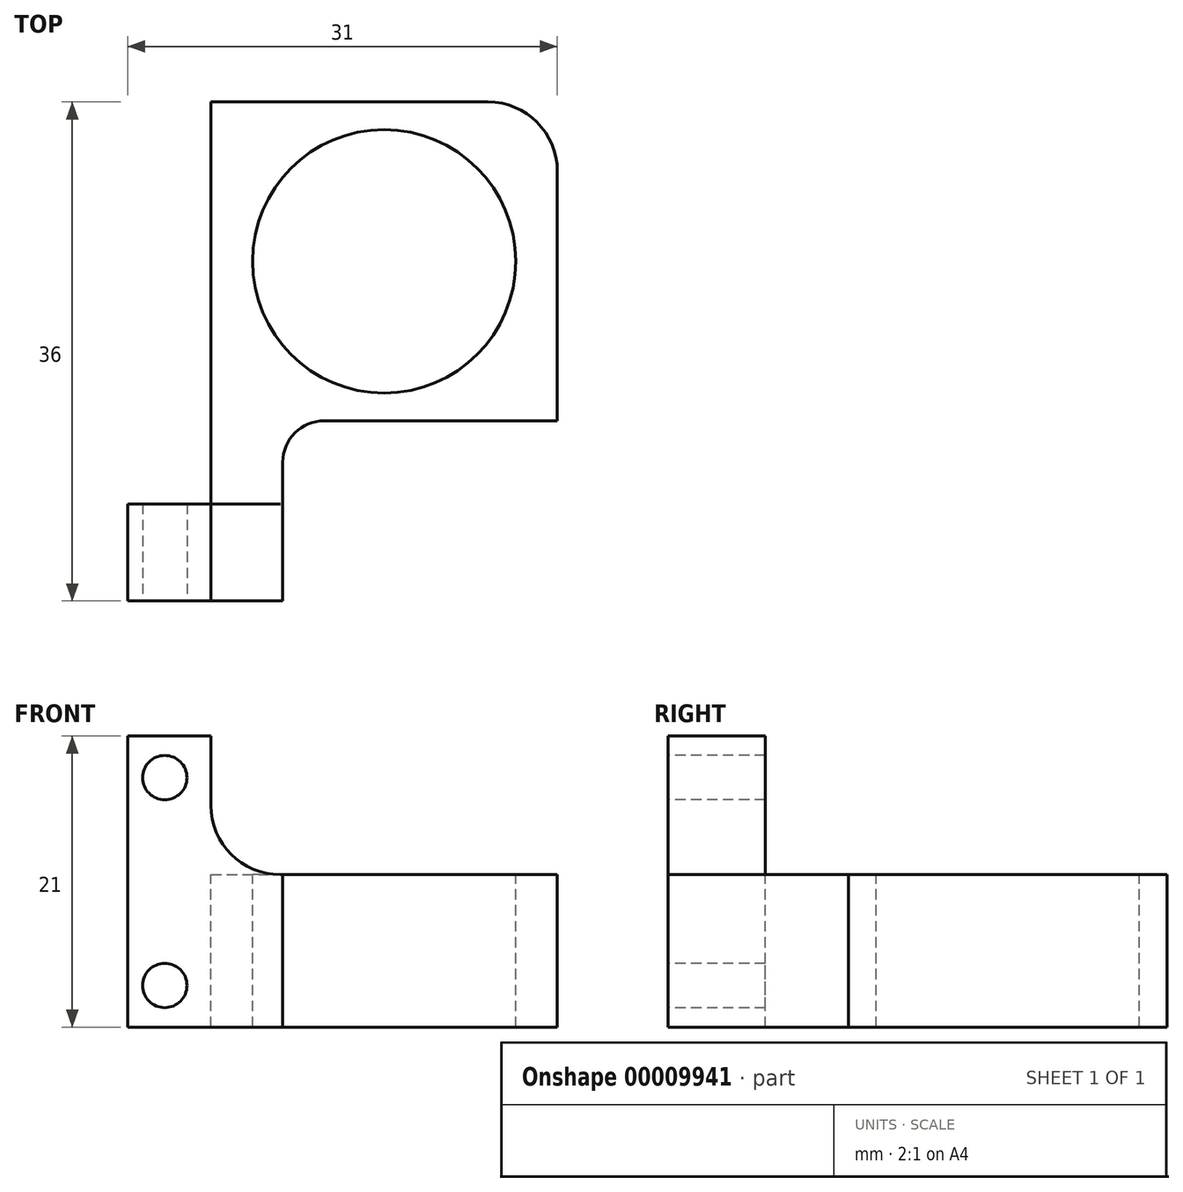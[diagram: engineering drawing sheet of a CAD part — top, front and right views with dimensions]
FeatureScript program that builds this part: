
annotation { "Feature Type Name" : "Feature", "Feature Type Description" : "" }
export const myFeature = defineFeature(function(context is Context, id is Id, definition is map)
    precondition{}
    {
        {
            var Q0;
            Q0=qCreatedBy(makeId("Top.planeOp"),FACE);
            var sketch = newSketch(context, id + "F0", { "sketchPlane" : qUnion([Q0])});
            skLineSegment(sketch, "E0.bottom", {"start": v(0, 0) * mm, "end": v(31, 0) * mm});
            skLineSegment(sketch, "E0.top", {"start": v(0, 36) * mm, "end": v(31, 36) * mm});
            skLineSegment(sketch, "E0.left", {"start": v(0, 0) * mm, "end": v(0, 36) * mm});
            skLineSegment(sketch, "E0.right", {"start": v(31, 0) * mm, "end": v(31, 36) * mm});
            skSolve(sketch);
        }
        {
            var Q0;
            Q0 = qSketchRegion(id + "F0", true);
            extrude(context, id + "F1", {"entities" : qUnion([Q0]), "depth" : 4 * mm});
        }
        {
            var Q0;
            Q0=makeQuery(id+"F1.opExtrude","CAP_FACE",FACE,{"disambiguationData":[OSD([sQuery(id+"F0.wireOp",EDGE,"E0.bottom"),sQuery(id+"F0.wireOp",EDGE,"E0.top"),sQuery(id+"F0.wireOp",EDGE,"E0.left"),sQuery(id+"F0.wireOp",EDGE,"E0.right")])],"isStart":false});
            var sketch = newSketch(context, id + "F2", { "sketchPlane" : qUnion([Q0])});
            skCircle(sketch, "E1", {"center": v(18.5, 24.5) * mm, "radius": 9.5 * mm});
            skLineSegment(sketch, "E2.bottom", {"start": v(0, 36) * mm, "end": v(6, 36) * mm});
            skLineSegment(sketch, "E2.top", {"start": v(0, 7) * mm, "end": v(6, 7) * mm});
            skLineSegment(sketch, "E2.left", {"start": v(0, 36) * mm, "end": v(0, 7) * mm});
            skLineSegment(sketch, "E2.right", {"start": v(6, 36) * mm, "end": v(6, 7) * mm});
            skLineSegment(sketch, "E3.bottom", {"start": v(31, 0) * mm, "end": v(11.18, 0) * mm});
            skLineSegment(sketch, "E3.top", {"start": v(31, 13) * mm, "end": v(11.18, 13) * mm});
            skLineSegment(sketch, "E3.left", {"start": v(31, 0) * mm, "end": v(31, 13) * mm});
            skLineSegment(sketch, "E3.right", {"start": v(11.18, 0) * mm, "end": v(11.18, 13) * mm});
            skSolve(sketch);
        }
        {
            var Q0;
            Q0 = qSketchRegion(id + "F2", true);
            extrude(context, id + "F3", {"entities" : qUnion([Q0]), "operationType" : NewBodyOperationType.REMOVE, "oppositeDirection" : true, "depth" : 25 * mm});
        }
        {
            var Q0;
            Q0=makeQuery(id+"F1.opExtrude","CAP_FACE",FACE,{"disambiguationData":[OSD([sQuery(id+"F0.wireOp",EDGE,"E0.bottom"),sQuery(id+"F0.wireOp",EDGE,"E0.top"),sQuery(id+"F0.wireOp",EDGE,"E0.left"),sQuery(id+"F0.wireOp",EDGE,"E0.right")])],"isStart":false});
            var sketch = newSketch(context, id + "F4", { "sketchPlane" : qUnion([Q0])});
            skLineSegment(sketch, "E4.bottom", {"start": v(0, 7) * mm, "end": v(6, 7) * mm});
            skLineSegment(sketch, "E4.top", {"start": v(0, 0) * mm, "end": v(6, 0) * mm});
            skLineSegment(sketch, "E4.left", {"start": v(0, 7) * mm, "end": v(0, 0) * mm});
            skLineSegment(sketch, "E4.right", {"start": v(6, 7) * mm, "end": v(6, 0) * mm});
            skSolve(sketch);
        }
        {
            var Q0;
            Q0 = qSketchRegion(id + "F4", true);
            var Q1;
            {var subQ1=sQuery(id+"F4.wireOp",EDGE,"E4.right");Q1=makeQuery(id+"F4.imprint","IMPRINT",FACE,{"disambiguationData":[TD([[makeQuery(id+"F4.imprint","IMPRINT",EDGE,{"derivedFrom":subQ1}),1.0]])]});}
            extrude(context, id + "F5", {"entities" : qUnion([Q0, Q1]), "operationType" : NewBodyOperationType.ADD, "depth" : 7 * mm});
        }
        {
            var Q0;
            Q0=makeQuery(id+"F4.imprint","IMPRINT",FACE,{"disambiguationData":[TD([[makeQuery(id+"F4.imprint","IMPRINT",EDGE,{"derivedFrom":sQuery(id+"F4.wireOp",EDGE,"E4.bottom")}),-1.0]])]});
            extrude(context, id + "F6", {"entities" : qUnion([Q0]), "operationType" : NewBodyOperationType.ADD, "depth" : 17 * mm});
        }
        {
            var Q0;
            Q0=makeQuery(id+"F5.boolean.opBoolean","MERGE",FACE,{"derivedFrom":[makeQuery(id+"F1.opExtrude","SWEPT_FACE",FACE,{"disambiguationData":[OSD([sQuery(id+"F0.wireOp",EDGE,"E0.bottom")])]}),makeQuery(id+"F5.opExtrude","SWEPT_FACE",FACE,{"disambiguationData":[OSD([sQuery(id+"F4.wireOp",EDGE,"E4.top")])]})]});
            var sketch = newSketch(context, id + "F7", { "sketchPlane" : qUnion([Q0])});
            skLineSegment(sketch, "E5", {"start": v(2.68, 18) * mm, "end": v(2.68, 3) * mm});
            skCircle(sketch, "E6", {"center": v(2.68, 18) * mm, "radius": 1.6 * mm});
            skCircle(sketch, "E7", {"center": v(2.68, 3) * mm, "radius": 1.6 * mm});
            skSolve(sketch);
        }
        {
            var Q0;
            Q0 = qSketchRegion(id + "F7", true);
            extrude(context, id + "F8", {"entities" : qUnion([Q0]), "operationType" : NewBodyOperationType.REMOVE, "oppositeDirection" : true, "depth" : 25 * mm});
        }
        {
            var Q0;
            Q0=makeQuery(id+"F1.opExtrude","SWEPT_EDGE",EDGE,{"disambiguationData":[OSD([sQuery(id+"F0.wireOp",EDGE,"E0.bottom"),sQuery(id+"F0.wireOp",EDGE,"E0.right")])]});
            var Q1;
            Q1=makeQuery(id+"F1.opExtrude","SWEPT_EDGE",EDGE,{"disambiguationData":[OSD([sQuery(id+"F0.wireOp",EDGE,"E0.top"),sQuery(id+"F0.wireOp",EDGE,"E0.right")])]});
            var Q2;
            Q2=makeQuery(id+"F3.boolean.opBoolean","COPY",EDGE,{"derivedFrom":makeQuery(id+"F3.opExtrude","SWEPT_EDGE",EDGE,{"disambiguationData":[OSD([sQuery(id+"F0.wireOp",EDGE,"E0.top"),sQuery(id+"F2.wireOp",EDGE,"E2.bottom"),sQuery(id+"F2.wireOp",EDGE,"E2.right")])]})});
            var Q3;
            Q3=makeQuery(id+"F3.boolean.opBoolean","COPY",EDGE,{"derivedFrom":makeQuery(id+"F3.opExtrude","SWEPT_EDGE",EDGE,{"disambiguationData":[OSD([sQuery(id+"F0.wireOp",EDGE,"E0.right"),sQuery(id+"F2.wireOp",EDGE,"E3.top"),sQuery(id+"F2.wireOp",EDGE,"E3.left")])]})});
            fillet(context, id + "F9", {"entities" : qUnion([Q0, Q1, Q2, Q3]), "radius" : 5 * mm, "tangentPropagation" : true, "allowEdgeOverflow" : false});
        }
        {
            var Q0;
            {var subQ0=sQuery(id+"F2.wireOp",EDGE,"E3.top");var subQ1=sQuery(id+"F2.wireOp",EDGE,"E3.right");Q0=makeQuery(id+"F5.boolean.opBoolean","MERGE",EDGE,{"derivedFrom":[makeQuery(id+"F3.boolean.opBoolean","COPY",EDGE,{"derivedFrom":makeQuery(id+"F3.opExtrude","SWEPT_EDGE",EDGE,{"disambiguationData":[OSD([subQ0,subQ1])]})}),makeQuery(id+"F5.opExtrude","SWEPT_EDGE",EDGE,{"disambiguationData":[OSD([subQ0,subQ1])]})]});}
            fillet(context, id + "F10", {"entities" : qUnion([Q0]), "radius" : 3 * mm, "tangentPropagation" : true, "allowEdgeOverflow" : false});
        }
        {
            var Q0;
            Q0=makeQuery(id+"F6.boolean.opBoolean","INTERSECT",EDGE,{"derivedFrom":[makeQuery(id+"F5.opExtrude","CAP_FACE",FACE,{"disambiguationData":[OSD([sQuery(id+"F0.wireOp",EDGE,"E0.bottom"),sQuery(id+"F0.wireOp",EDGE,"E0.top"),sQuery(id+"F0.wireOp",EDGE,"E0.right"),sQuery(id+"F2.wireOp",EDGE,"E1"),sQuery(id+"F2.wireOp",EDGE,"E2.right"),sQuery(id+"F2.wireOp",EDGE,"E3.top"),sQuery(id+"F2.wireOp",EDGE,"E3.right"),sQuery(id+"F4.wireOp",EDGE,"E4.bottom"),sQuery(id+"F4.wireOp",EDGE,"E4.top"),sQuery(id+"F4.wireOp",EDGE,"E4.left")])],"isStart":false}),makeQuery(id+"F6.opExtrude","SWEPT_FACE",FACE,{"disambiguationData":[OSD([sQuery(id+"F4.wireOp",EDGE,"E4.right")])]})]});
            fillet(context, id + "F11", {"entities" : qUnion([Q0]), "radius" : 5 * mm, "tangentPropagation" : true, "allowEdgeOverflow" : false});
        }
    });
